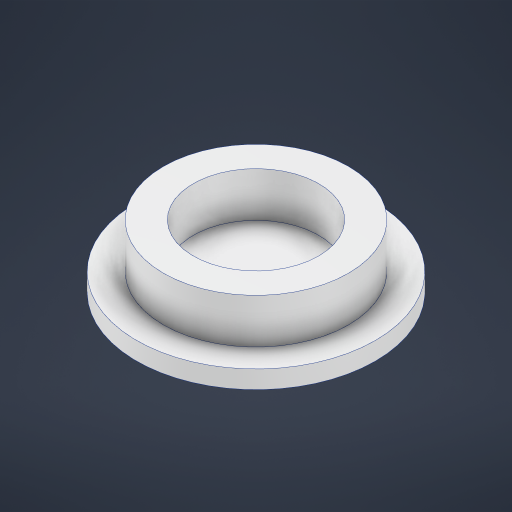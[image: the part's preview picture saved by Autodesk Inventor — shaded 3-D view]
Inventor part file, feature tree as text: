
AUTODESK INVENTOR PART (.ipt)
format: ipt  version: 2024 (Build 280153000, 153)  size: 378,880 bytes
history: native  units: mm
features: extrude x4, sketch x4, pattern_circular x1, projected_geometry x1
ambient origin geometry x8: Origin, YZ Plane, XZ Plane, XY Plane, X Axis, Y Axis, Z Axis, Center Point
bodies: Solid1 (feature_tree)
feature tree (10):
  extrude  "Extrusion1"  Depth=12.0mm TaperAngle=0.0deg
  extrude  "Extrusion2"  Depth=10.0mm TaperAngle=0.0deg
  extrude  "Extrusion3"  Depth=14.0mm TaperAngle=0.0deg
  pattern_circular  "Circular Pattern1"  Count=16  [1 undecoded]
  extrude  "Extrusion4"  [1 undecoded]
  sketch  "Sketch1"  dims[d0=250.0mm d1=12.0mm d2=0.0mm]
  sketch  "Sketch2"  dims[d3=30.0mm d4=0.0mm d5=10.0mm d6=0.0mm]
  projected_geometry  "Projected Loop1"
  sketch  "Sketch3"  dims[d7=1800.0mm d8=360.0deg d10=14.0mm d11=0.0mm d12=160.0mm]
  sketch  "Sketch4"
note: 2 required parameter values undecoded (feature->parameter linkage not recoverable at this tier; creation-order binding heuristic only, values carry confidence <= 0.55)
